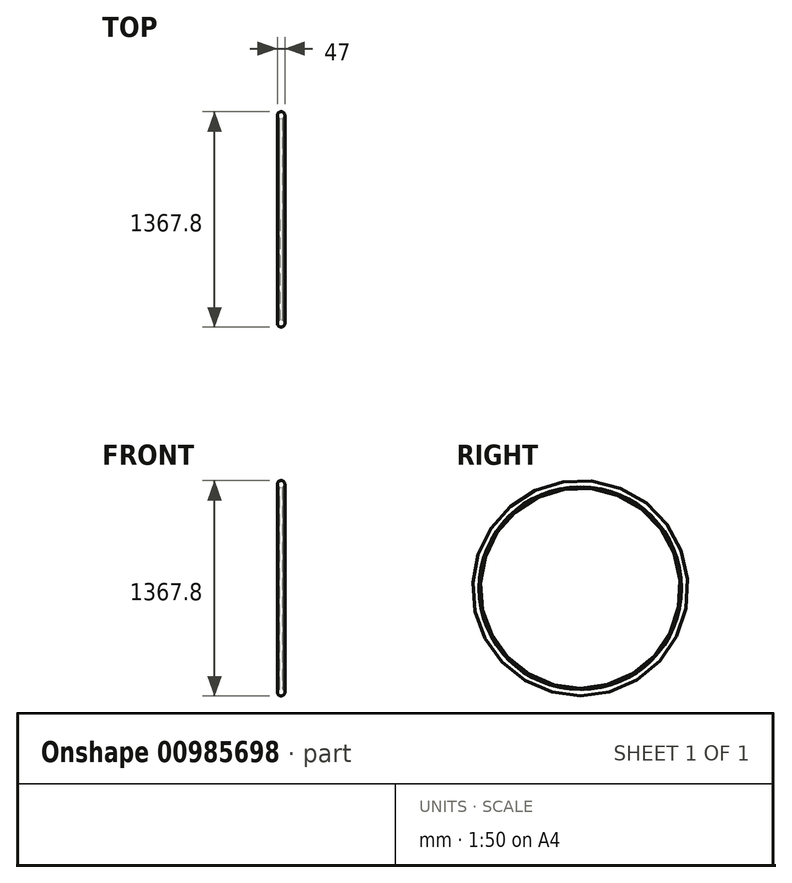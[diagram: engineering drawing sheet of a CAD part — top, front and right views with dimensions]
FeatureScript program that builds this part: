
annotation { "Feature Type Name" : "Feature", "Feature Type Description" : "" }
export const myFeature = defineFeature(function(context is Context, id is Id, definition is map)
    precondition{}
    {
        {
            var Q0;
            Q0=qCreatedBy(makeId("Front.planeOp"),FACE);
            var sketch = newSketch(context, id + "F0", { "sketchPlane" : qUnion([Q0])});
            skArc(sketch, "E0", {"start": v(11.64, 641.46) * mm, "mid": v(11.9, 635.9) * mm, "end": v(16.45, 639.12) * mm});
            skArc(sketch, "E1", {"start": v(-16.26, 639.9) * mm, "mid": v(-12.28, 635.75) * mm, "end": v(-11.64, 641.46) * mm});
            skFitSpline(sketch, "E2", {"points": [v(-16.47, 638.89) * mm, v(-16.8, 645.84) * mm, v(-34.3, 656.83) * mm], "startDerivative": vector(4.07, 19.24) * mm, "endDerivative": vector(-36.18, 16.85) * mm});
            skFitSpline(sketch, "E3", {"points": [v(16.47, 639) * mm, v(17.59, 646.82) * mm, v(30.94, 651.17) * mm], "startDerivative": vector(-1.93, 20.56) * mm, "endDerivative": vector(29.34, 4.55) * mm});
            skArc(sketch, "E4", {"start": v(11.64, 641.46) * mm, "mid": v(0, 682.62) * mm, "end": v(-11.64, 641.46) * mm});
            skArc(sketch, "E5", {"start": v(16.33, 643.5) * mm, "mid": v(-0.24, 683.9) * mm, "end": v(-15.97, 643.17) * mm});
            skSolve(sketch);
        }
        {
            var Q0;
            Q0=qCreatedBy(makeId("Top.planeOp"),FACE);
            var sketch = newSketch(context, id + "F1", { "sketchPlane" : qUnion([Q0])});
            skLineSegment(sketch, "E6", {"start": v(0, 0) * mm, "end": v(-67.21, 0) * mm});
            skSolve(sketch);
        }
        {
            var Q0;
            Q0 = qSketchRegion(id + "F0", true);
            var Q1;
            Q1=sQuery(id+"F1.wireOp",EDGE,"E6");
            revolve(context, id + "F2", {"surfaceOperationType" : NewSurfaceOperationType.NEW, "entities" : qUnion([Q0]), "axis" : qUnion([Q1]), "revolveType" : RevolveType.FULL});
        }
    });
